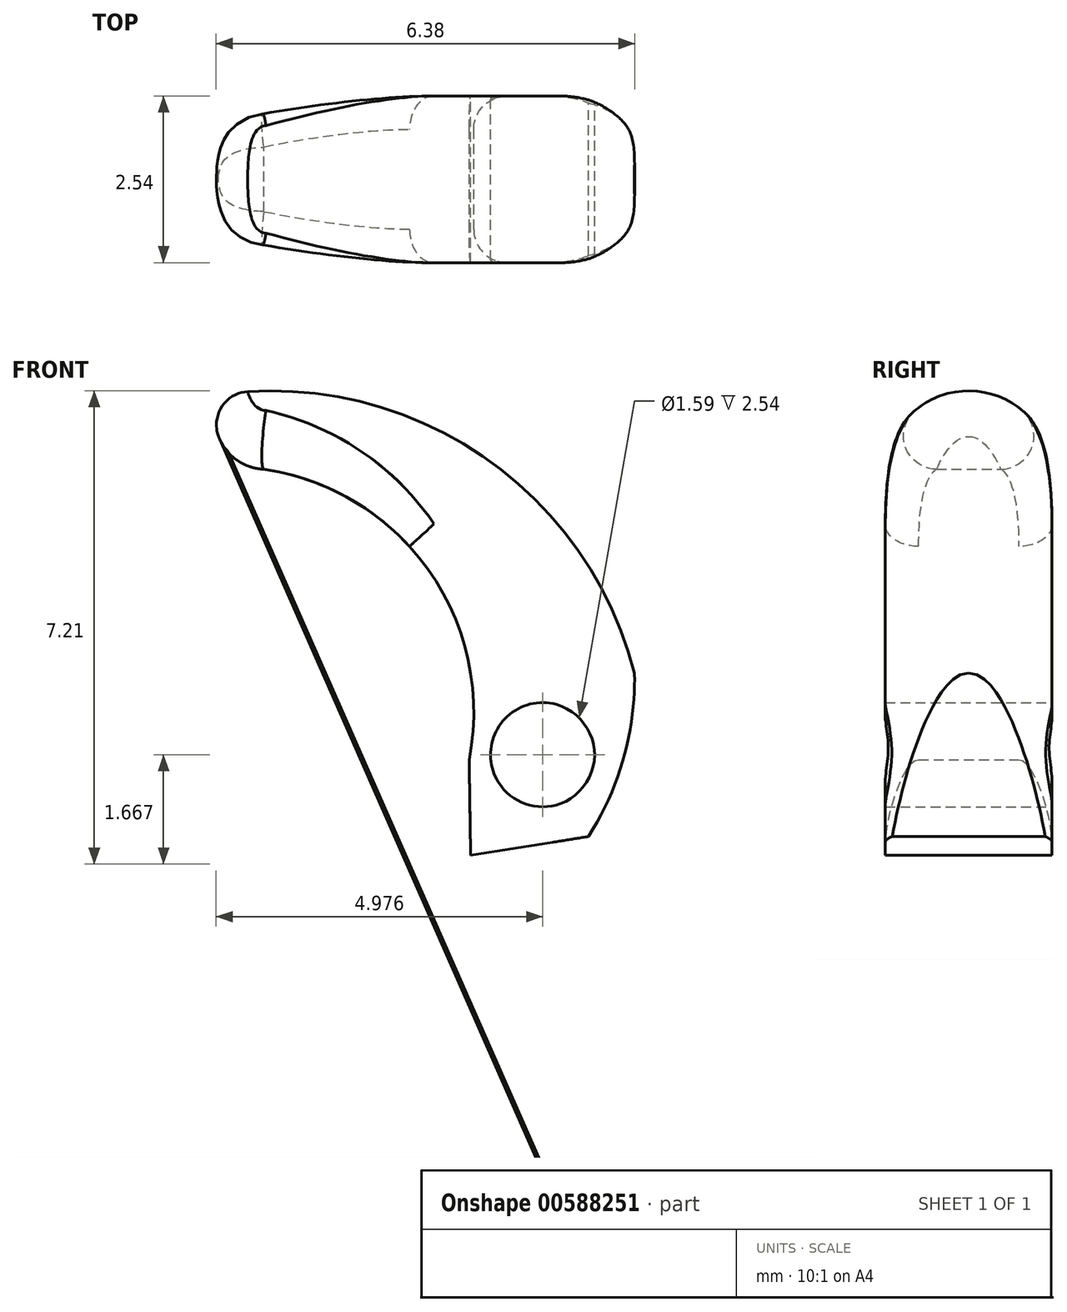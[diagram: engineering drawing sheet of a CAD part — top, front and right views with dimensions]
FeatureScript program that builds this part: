
annotation { "Feature Type Name" : "Feature", "Feature Type Description" : "" }
export const myFeature = defineFeature(function(context is Context, id is Id, definition is map)
    precondition{}
    {
        {
            var Q0;
            Q0=qCreatedBy(makeId("Front.planeOp"),FACE);
            var sketch = newSketch(context, id + "F0", { "sketchPlane" : qUnion([Q0])});
            skPoint(sketch, "E0", {"position": v(-15.97, 34.1) * mm});
            skPoint(sketch, "E1", {"position": v(-15.97, 48.78) * mm});
            skPoint(sketch, "E2.positionSnap0", {"position": v(-13.33, 37.13) * mm});
            skPoint(sketch, "E3", {"position": v(-8.85, 43) * mm});
            skPoint(sketch, "E4.endSnap0", {"position": v(-10.05, 42.5) * mm});
            skArc(sketch, "E5", {"start": v(-7.45, 44.24) * mm, "mid": v(-9.8, 47.56) * mm, "end": v(-13.74, 48.5) * mm});
            skArc(sketch, "E6", {"start": v(-8.16, 41.75) * mm, "mid": v(-7.62, 42.94) * mm, "end": v(-7.45, 44.24) * mm});
            skArc(sketch, "E7", {"start": v(-13.74, 48.5) * mm, "mid": v(-13.74, 47.74) * mm, "end": v(-13.1, 47.34) * mm});
            skLineSegment(sketch, "E8", {"start": v(-9.95, 41.46) * mm, "end": v(-9.97, 42.92) * mm});
            skArc(sketch, "E9", {"start": v(-9.97, 42.92) * mm, "mid": v(-10.6, 45.8) * mm, "end": v(-13.1, 47.34) * mm});
            skLineSegment(sketch, "E10", {"start": v(-9.95, 41.46) * mm, "end": v(-8.16, 41.75) * mm});
            skSolve(sketch);
        }
        {
            var Q0;
            Q0=makeQuery(id+"F0.imprint","IMPRINT",FACE,{"disambiguationData":[TD([[makeQuery(id+"F0.imprint","IMPRINT",EDGE,{"derivedFrom":sQuery(id+"F0.wireOp",EDGE,"1fGJHQu9-igq8-0Tgg-verT-ZQO9qWZd8SWi")}),1.0]])]});
            var Q1;
            Q1=makeQuery(id+"F0.imprint","IMPRINT",FACE,{"disambiguationData":[TD([[makeQuery(id+"F0.imprint","IMPRINT",EDGE,{"derivedFrom":sQuery(id+"F0.wireOp",EDGE,"qE8Chysm-J05S-KyC3-tMCQ-S1st76Zv7HF8")}),-1.0]])]});
            var Q2;
            Q2=makeQuery(id+"F0.imprint","IMPRINT",FACE,{"disambiguationData":[TD([[makeQuery(id+"F0.imprint","IMPRINT",EDGE,{"derivedFrom":sQuery(id+"F0.wireOp",EDGE,"wdI1CQQ0-s7A4-k37b-cujT-hYxwutjPY7WN")}),1.0]])]});
            var Q3;
            Q3=makeQuery(id+"F0.imprint","IMPRINT",FACE,{"disambiguationData":[TD([[makeQuery(id+"F0.imprint","IMPRINT",EDGE,{"derivedFrom":sQuery(id+"F0.wireOp",EDGE,"DZVlWGr7-4dgk-KfWk-qw7t-reTPJHtmkTbP")}),1.0]])]});
            var Q4;
            Q4=makeQuery(id+"F0.imprint","IMPRINT",FACE,{"disambiguationData":[TD([[makeQuery(id+"F0.imprint","IMPRINT",EDGE,{"derivedFrom":sQuery(id+"F0.wireOp",EDGE,"qeftRayW-Si8I-tjzs-Cj9I-jnzv1c80Uy4t")}),1.0]])]});
            var Q5;
            Q5=makeQuery(id+"F0.imprint","IMPRINT",FACE,{"disambiguationData":[TD([[makeQuery(id+"F0.imprint","IMPRINT",EDGE,{"derivedFrom":sQuery(id+"F0.wireOp",EDGE,"BQxfKqpF-ZsrL-QiEq-6Z18-1x3xAn4C3XR2")}),-1.0]])]});
            var Q6;
            Q6=makeQuery(id+"F0.imprint","IMPRINT",FACE,{"disambiguationData":[TD([[makeQuery(id+"F0.imprint","IMPRINT",EDGE,{"derivedFrom":sQuery(id+"F0.wireOp",EDGE,"E5")}),1.0]])]});
            extrude(context, id + "F1", {"entities" : qUnion([Q0, Q1, Q2, Q3, Q4, Q5, Q6]), "depth" : 2.54 * mm, "offsetDistance" : 25.4 * mm});
        }
        {
            var Q0;
            Q0=sQuery(id+"F0.wireOp",VERTEX,"E3");
            var Q1;
            Q1=makeQuery(id+"F1.opExtrude","SWEPT_BODY",BODY,{"disambiguationData":[OSD([sQuery(id+"F0.wireOp",EDGE,"BQxfKqpF-ZsrL-QiEq-6Z18-1x3xAn4C3XR2"),sQuery(id+"F0.wireOp",EDGE,"E5"),sQuery(id+"F0.wireOp",EDGE,"E6"),sQuery(id+"F0.wireOp",EDGE,"KY4dQEa4-AzTi-2BSd-hZcb-fizEvPymQtwp"),sQuery(id+"F0.wireOp",EDGE,"E7"),sQuery(id+"F0.wireOp",EDGE,"kDAmfD9L-abeQ-a5wv-ccu2-a4rihuRBV7d8")])]});
            hole(context, id + "F2", {"style" : HoleStyle.SIMPLE, "endStyle" : HoleEndStyle.THROUGH, "oppositeDirection" : true, "holeDiameter" : 1.59 * mm, "majorDiameter" : 6.35 * mm, "isTappedThrough" : true, "tappedDepth" : 12.7 * mm, "tapClearance" : 3, "locations" : qUnion([Q0]), "scope" : qUnion([Q1])});
        }
        {
            var Q0;
            Q0=makeQuery(id+"F1.opExtrude","CAP_EDGE",EDGE,{"disambiguationData":[OSD([sQuery(id+"F0.wireOp",EDGE,"E5")])],"isStart":true});
            var Q1;
            Q1=makeQuery(id+"F1.opExtrude","CAP_EDGE",EDGE,{"disambiguationData":[OSD([sQuery(id+"F0.wireOp",EDGE,"E5")])],"isStart":false});
            fillet(context, id + "F3", {"entities" : qUnion([Q0, Q1]), "radius" : 1.27 * mm, "tangentPropagation" : true, "allowEdgeOverflow" : false});
        }
        {
            var Q0;
            Q0=makeQuery(id+"F1.opExtrude","CAP_EDGE",EDGE,{"disambiguationData":[OSD([sQuery(id+"F0.wireOp",EDGE,"E9")])],"isStart":true});
            var Q1;
            Q1=makeQuery(id+"F1.opExtrude","CAP_EDGE",EDGE,{"disambiguationData":[OSD([sQuery(id+"F0.wireOp",EDGE,"E9")])],"isStart":false});
            var Q2;
            Q2=makeQuery(id+"F3.opFillet","BLEND_EDGE",EDGE,{"blendedFrom":[makeQuery(id+"F1.opExtrude","CAP_EDGE",EDGE,{"disambiguationData":[OSD([sQuery(id+"F0.wireOp",EDGE,"E5")])],"isStart":true}),makeQuery(id+"F1.opExtrude","SWEPT_FACE",FACE,{"disambiguationData":[OSD([sQuery(id+"F0.wireOp",EDGE,"E7")])]})],"blendedInto":[makeQuery(id+"F1.opExtrude","SWEPT_FACE",FACE,{"disambiguationData":[OSD([sQuery(id+"F0.wireOp",EDGE,"E7")])]})]});
            var Q3;
            Q3=makeQuery(id+"F3.opFillet","BLEND_EDGE",EDGE,{"blendedFrom":[makeQuery(id+"F1.opExtrude","CAP_EDGE",EDGE,{"disambiguationData":[OSD([sQuery(id+"F0.wireOp",EDGE,"E5")])],"isStart":false}),makeQuery(id+"F1.opExtrude","SWEPT_FACE",FACE,{"disambiguationData":[OSD([sQuery(id+"F0.wireOp",EDGE,"E7")])]})],"blendedInto":[makeQuery(id+"F1.opExtrude","SWEPT_FACE",FACE,{"disambiguationData":[OSD([sQuery(id+"F0.wireOp",EDGE,"E7")])]})]});
            fillet(context, id + "F4", {"entities" : qUnion([Q0, Q1, Q2, Q3]), "radius" : 0.5 * mm, "tangentPropagation" : true, "allowEdgeOverflow" : false});
        }
        {
            var Q0;
            Q0=makeQuery(id+"F1.opExtrude","SWEPT_BODY",BODY,{"disambiguationData":[OSD([sQuery(id+"F0.wireOp",EDGE,"E5"),sQuery(id+"F0.wireOp",EDGE,"E6"),sQuery(id+"F0.wireOp",EDGE,"E7"),sQuery(id+"F0.wireOp",EDGE,"E8"),sQuery(id+"F0.wireOp",EDGE,"E9"),sQuery(id+"F0.wireOp",EDGE,"E10")])]});
            var Q1;
            Q1=sQuery(id+"F0.wireOp",VERTEX,"E10.start");
            transform(context, id + "F5", {"entities" : qUnion([Q0]), "transformType" : TransformType.SCALE_UNIFORMLY, "scale" : 1, "scalePoint" : qUnion([Q1]), "makeCopy" : false});
        }
    });
